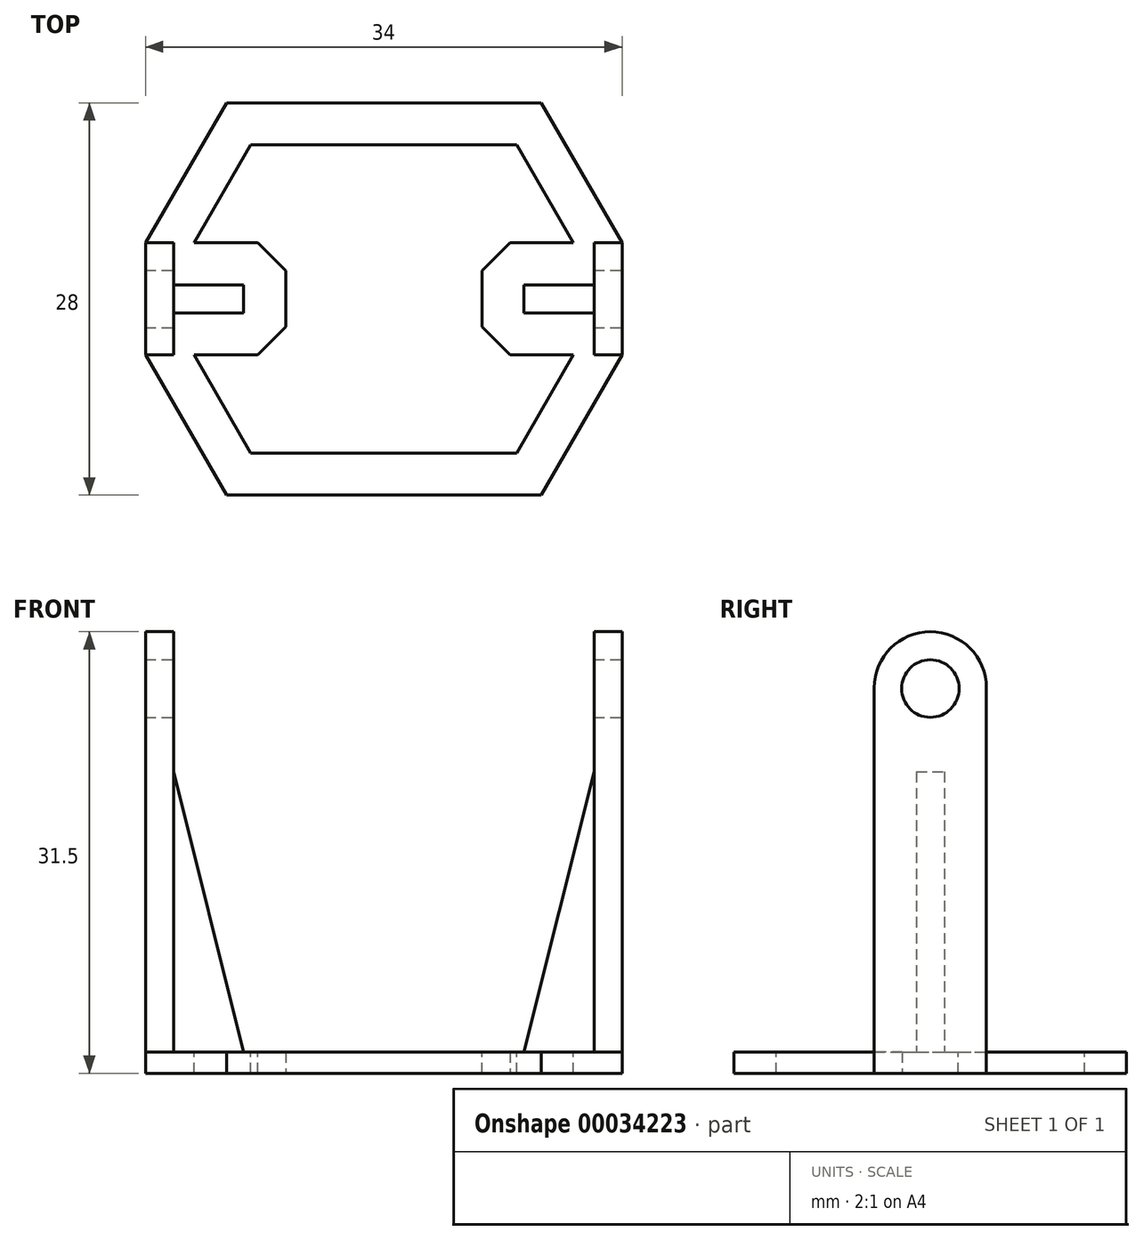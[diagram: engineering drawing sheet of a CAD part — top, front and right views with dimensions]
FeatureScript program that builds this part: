
annotation { "Feature Type Name" : "Feature", "Feature Type Description" : "" }
export const myFeature = defineFeature(function(context is Context, id is Id, definition is map)
    precondition{}
    {
        {
            var Q0;
            Q0=qCreatedBy(makeId("Front.planeOp"),FACE);
            var sketch = newSketch(context, id + "F0", { "sketchPlane" : qUnion([Q0])});
            skLineSegment(sketch, "E0", {"start": v(0, 0) * mm, "end": v(15, 0) * mm});
            skLineSegment(sketch, "E1", {"start": v(17, -1.5) * mm, "end": v(0, -1.5) * mm});
            skLineSegment(sketch, "E2", {"start": v(0, 0.66) * mm, "end": v(0, 21.18) * mm, "construction": true});
            skLineSegment(sketch, "E3", {"start": v(17, 30) * mm, "end": v(15, 30) * mm});
            skLineSegment(sketch, "E4", {"start": v(15, 30) * mm, "end": v(15, 0) * mm});
            skLineSegment(sketch, "E5", {"start": v(17, -1.5) * mm, "end": v(17, 30) * mm});
            skLineSegment(sketch, "E6.MirrorCS", {"start": v(-17, -1.5) * mm, "end": v(0, -1.5) * mm});
            skLineSegment(sketch, "E7.MirrorCS", {"start": v(-17, 30) * mm, "end": v(-15, 30) * mm});
            skLineSegment(sketch, "E8.MirrorCS", {"start": v(-15, 30) * mm, "end": v(-15, 0) * mm});
            skLineSegment(sketch, "E9.MirrorCS", {"start": v(0, 0) * mm, "end": v(-15, 0) * mm});
            skLineSegment(sketch, "E10.MirrorCS", {"start": v(-17, -1.5) * mm, "end": v(-17, 30) * mm});
            skSolve(sketch);
        }
        {
            var Q0;
            Q0=makeQuery(id+"F0.imprint","IMPRINT",FACE,{"disambiguationData":[TD([[makeQuery(id+"F0.imprint","IMPRINT",EDGE,{"derivedFrom":sQuery(id+"F0.wireOp",EDGE,"E0")}),-1.0]])]});
            extrude(context, id + "F1", {"entities" : qUnion([Q0]), "endBound" : BoundingType.SYMMETRIC, "depth" : 8 * mm});
        }
        {
            var Q0;
            Q0=makeQuery(id+"F1.opExtrude","SWEPT_FACE",FACE,{"disambiguationData":[OSD([sQuery(id+"F0.wireOp",EDGE,"E5")])]});
            var sketch = newSketch(context, id + "F2", { "sketchPlane" : qUnion([Q0])});
            skCircle(sketch, "E11", {"center": v(0, 25.95) * mm, "radius": 2.05 * mm});
            skSolve(sketch);
        }
        {
            var Q0;
            Q0=makeQuery(id+"F2.imprint","IMPRINT",FACE,{"disambiguationData":[TD([[makeQuery(id+"F2.imprint","IMPRINT",EDGE,{"derivedFrom":sQuery(id+"F2.wireOp",EDGE,"E11")}),1.0]])]});
            extrude(context, id + "F3", {"entities" : qUnion([Q0]), "operationType" : NewBodyOperationType.REMOVE, "endBound" : BoundingType.THROUGH_ALL, "oppositeDirection" : true, "depth" : 25 * mm});
        }
        {
            var Q0;
            Q0=qCreatedBy(makeId("Front.planeOp"),FACE);
            var sketch = newSketch(context, id + "F4", { "sketchPlane" : qUnion([Q0])});
            skLineSegment(sketch, "E12.0", {"start": v(-15, 30) * mm, "end": v(-15, 0) * mm});
            skLineSegment(sketch, "E13.0", {"start": v(-15, 0) * mm, "end": v(15, 0) * mm});
            skLineSegment(sketch, "E14.0", {"start": v(15, 30) * mm, "end": v(15, 0) * mm});
            skLineSegment(sketch, "E15", {"start": v(-15, 20) * mm, "end": v(-10, 0) * mm});
            skLineSegment(sketch, "E16", {"start": v(-10, 0) * mm, "end": v(-15, 0) * mm});
            skLineSegment(sketch, "E17", {"start": v(-15, 20) * mm, "end": v(-15, 0) * mm});
            skLineSegment(sketch, "E18.MirrorCS", {"start": v(10, 0) * mm, "end": v(15, 0) * mm});
            skLineSegment(sketch, "E19.MirrorCS", {"start": v(15, 20) * mm, "end": v(10, 0) * mm});
            skLineSegment(sketch, "E20.MirrorCS", {"start": v(15, 20) * mm, "end": v(15, 0) * mm});
            skSolve(sketch);
        }
        {
            var Q0;
            Q0=makeQuery(id+"F4.imprint","IMPRINT",FACE,{"disambiguationData":[TD([[makeQuery(id+"F4.imprint","IMPRINT",EDGE,{"derivedFrom":sQuery(id+"F4.wireOp",EDGE,"E15")}),-1.0]])]});
            var Q1;
            Q1=makeQuery(id+"F4.imprint","IMPRINT",FACE,{"disambiguationData":[TD([[makeQuery(id+"F4.imprint","IMPRINT",EDGE,{"derivedFrom":sQuery(id+"F4.wireOp",EDGE,"E19.MirrorCS")}),1.0]])]});
            extrude(context, id + "F5", {"entities" : qUnion([Q0, Q1]), "operationType" : NewBodyOperationType.ADD, "endBound" : BoundingType.SYMMETRIC, "depth" : 2 * mm});
        }
        {
            var Q0;
            Q0=makeQuery(id+"F1.opExtrude","SWEPT_FACE",FACE,{"disambiguationData":[OSD([sQuery(id+"F0.wireOp",EDGE,"E0"),sQuery(id+"F0.wireOp",EDGE,"E9.MirrorCS")])]});
            var sketch = newSketch(context, id + "F6", { "sketchPlane" : qUnion([Q0])});
            skPoint(sketch, "E21.0", {"position": v(-17, 4) * mm});
            skPoint(sketch, "E22.0", {"position": v(17, 4) * mm});
            skLineSegment(sketch, "E23", {"start": v(-17, 4) * mm, "end": v(-11.23, 14) * mm});
            skLineSegment(sketch, "E24", {"start": v(-11.23, 14) * mm, "end": v(0, 14) * mm});
            skLineSegment(sketch, "E25.MirrorCS", {"start": v(17, 4) * mm, "end": v(11.23, 14) * mm});
            skLineSegment(sketch, "E26.MirrorCS", {"start": v(11.23, 14) * mm, "end": v(0, 14) * mm});
            skPoint(sketch, "E27.MirrorP", {"position": v(17, -4) * mm});
            skPoint(sketch, "E28.MirrorP", {"position": v(-17, -4) * mm});
            skLineSegment(sketch, "E29.MirrorCS", {"start": v(11.23, -14) * mm, "end": v(0, -14) * mm});
            skLineSegment(sketch, "E30.MirrorCS", {"start": v(17, -4) * mm, "end": v(11.23, -14) * mm});
            skLineSegment(sketch, "E31.MirrorCS", {"start": v(-17, -4) * mm, "end": v(-11.23, -14) * mm});
            skLineSegment(sketch, "E32.MirrorCS", {"start": v(-11.23, -14) * mm, "end": v(0, -14) * mm});
            skLineSegment(sketch, "E33", {"start": v(-17, 4) * mm, "end": v(17, 4) * mm});
            skLineSegment(sketch, "E34", {"start": v(17, -4) * mm, "end": v(-17, -4) * mm});
            skSolve(sketch);
        }
        {
            var Q0;
            Q0=makeQuery(id+"F6.imprint","IMPRINT",FACE,{"disambiguationData":[TD([[makeQuery(id+"F6.imprint","IMPRINT",EDGE,{"derivedFrom":sQuery(id+"F6.wireOp",EDGE,"E29.MirrorCS")}),-1.0]])]});
            var Q1;
            {var subQ9=sQuery(id+"F6.wireOp",EDGE,"E23");Q1=makeQuery(id+"F6.imprint","IMPRINT",FACE,{"disambiguationData":[TD([[makeQuery(id+"F6.imprint","IMPRINT",EDGE,{"derivedFrom":subQ9}),-1.0]])]});}
            var Q2;
            Q2=makeQuery(id+"F1.opExtrude","SWEPT_FACE",FACE,{"disambiguationData":[OSD([sQuery(id+"F0.wireOp",EDGE,"E1"),sQuery(id+"F0.wireOp",EDGE,"E6.MirrorCS")])]});
            extrude(context, id + "F7", {"entities" : qUnion([Q0, Q1]), "operationType" : NewBodyOperationType.ADD, "endBound" : BoundingType.UP_TO_SURFACE, "oppositeDirection" : true, "endBoundEntityFace" : qUnion([Q2]), "depth" : 25 * mm});
        }
        {
            var Q0;
            Q0=makeQuery(id+"F7.boolean.opBoolean","MERGE",FACE,{"derivedFrom":[makeQuery(id+"F1.opExtrude","SWEPT_FACE",FACE,{"disambiguationData":[OSD([sQuery(id+"F0.wireOp",EDGE,"E0"),sQuery(id+"F0.wireOp",EDGE,"E9.MirrorCS")])]}),makeQuery(id+"F7.opExtrude","CAP_FACE",FACE,{"disambiguationData":[OSD([sQuery(id+"F6.wireOp",EDGE,"E23"),sQuery(id+"F6.wireOp",EDGE,"E24"),sQuery(id+"F6.wireOp",EDGE,"E25.MirrorCS"),sQuery(id+"F6.wireOp",EDGE,"E26.MirrorCS"),sQuery(id+"F6.wireOp",EDGE,"E33")])],"isStart":true}),makeQuery(id+"F7.opExtrude","CAP_FACE",FACE,{"disambiguationData":[OSD([sQuery(id+"F6.wireOp",EDGE,"E29.MirrorCS"),sQuery(id+"F6.wireOp",EDGE,"E30.MirrorCS"),sQuery(id+"F6.wireOp",EDGE,"E31.MirrorCS"),sQuery(id+"F6.wireOp",EDGE,"E32.MirrorCS"),sQuery(id+"F6.wireOp",EDGE,"E34")])],"isStart":true})]});
            var sketch = newSketch(context, id + "F8", { "sketchPlane" : qUnion([Q0])});
            skLineSegment(sketch, "E35.1", {"start": v(-13.54, -4) * mm, "end": v(-9.5, -11) * mm});
            skLineSegment(sketch, "E35.2", {"start": v(9.5, -11) * mm, "end": v(-9.5, -11) * mm});
            skLineSegment(sketch, "E35.3", {"start": v(13.54, -4) * mm, "end": v(9.5, -11) * mm});
            skLineSegment(sketch, "E35.5", {"start": v(-13.54, 4) * mm, "end": v(-9.5, 11) * mm});
            skLineSegment(sketch, "E35.6", {"start": v(13.54, 4) * mm, "end": v(9.5, 11) * mm});
            skLineSegment(sketch, "E35.7", {"start": v(9.5, 11) * mm, "end": v(-9.5, 11) * mm});
            skLineSegment(sketch, "E36.0", {"start": v(-13.54, -4) * mm, "end": v(-7, -4) * mm});
            skLineSegment(sketch, "E36.1", {"start": v(-7, -4) * mm, "end": v(-7, 4) * mm});
            skLineSegment(sketch, "E36.2", {"start": v(-13.54, 4) * mm, "end": v(-7, 4) * mm});
            skLineSegment(sketch, "E37.0", {"start": v(13.54, -4) * mm, "end": v(7, -4) * mm});
            skLineSegment(sketch, "E37.1", {"start": v(7, -4) * mm, "end": v(7, 4) * mm});
            skLineSegment(sketch, "E37.2", {"start": v(13.54, 4) * mm, "end": v(7, 4) * mm});
            skSolve(sketch);
        }
        {
            var Q0;
            Q0=makeQuery(id+"F8.imprint","IMPRINT",FACE,{"disambiguationData":[TD([[makeQuery(id+"F8.imprint","IMPRINT",EDGE,{"derivedFrom":sQuery(id+"F8.wireOp",EDGE,"E35.1")}),1.0]])]});
            extrude(context, id + "F9", {"entities" : qUnion([Q0]), "operationType" : NewBodyOperationType.REMOVE, "endBound" : BoundingType.THROUGH_ALL, "oppositeDirection" : true, "depth" : 25 * mm});
        }
        {
            var Q0;
            Q0=makeQuery(id+"F9.boolean.opBoolean","COPY",EDGE,{"derivedFrom":makeQuery(id+"F9.opExtrude","SWEPT_EDGE",EDGE,{"disambiguationData":[OSD([sQuery(id+"F8.wireOp",EDGE,"E36.0"),sQuery(id+"F8.wireOp",EDGE,"E36.1")])]})});
            var Q1;
            Q1=makeQuery(id+"F9.boolean.opBoolean","COPY",EDGE,{"derivedFrom":makeQuery(id+"F9.opExtrude","SWEPT_EDGE",EDGE,{"disambiguationData":[OSD([sQuery(id+"F8.wireOp",EDGE,"E36.1"),sQuery(id+"F8.wireOp",EDGE,"E36.2")])]})});
            var Q2;
            Q2=makeQuery(id+"F9.boolean.opBoolean","COPY",EDGE,{"derivedFrom":makeQuery(id+"F9.opExtrude","SWEPT_EDGE",EDGE,{"disambiguationData":[OSD([sQuery(id+"F8.wireOp",EDGE,"E37.0"),sQuery(id+"F8.wireOp",EDGE,"E37.1")])]})});
            var Q3;
            Q3=makeQuery(id+"F9.boolean.opBoolean","COPY",EDGE,{"derivedFrom":makeQuery(id+"F9.opExtrude","SWEPT_EDGE",EDGE,{"disambiguationData":[OSD([sQuery(id+"F8.wireOp",EDGE,"E37.1"),sQuery(id+"F8.wireOp",EDGE,"E37.2")])]})});
            chamfer(context, id + "F10", {"entities" : qUnion([Q0, Q1, Q2, Q3]), "width" : 2 * mm, "tangentPropagation" : true});
        }
        {
            var Q0;
            Q0=makeQuery(id+"F1.opExtrude","CAP_EDGE",EDGE,{"disambiguationData":[OSD([sQuery(id+"F0.wireOp",EDGE,"E7.MirrorCS")])],"isStart":false});
            var Q1;
            Q1=makeQuery(id+"F1.opExtrude","CAP_EDGE",EDGE,{"disambiguationData":[OSD([sQuery(id+"F0.wireOp",EDGE,"E3")])],"isStart":false});
            var Q2;
            Q2=makeQuery(id+"F1.opExtrude","CAP_EDGE",EDGE,{"disambiguationData":[OSD([sQuery(id+"F0.wireOp",EDGE,"E3")])],"isStart":true});
            var Q3;
            Q3=makeQuery(id+"F1.opExtrude","CAP_EDGE",EDGE,{"disambiguationData":[OSD([sQuery(id+"F0.wireOp",EDGE,"E7.MirrorCS")])],"isStart":true});
            fillet(context, id + "F11", {"entities" : qUnion([Q0, Q1, Q2, Q3]), "radius" : 4 * mm, "tangentPropagation" : true, "allowEdgeOverflow" : false});
        }
    });
